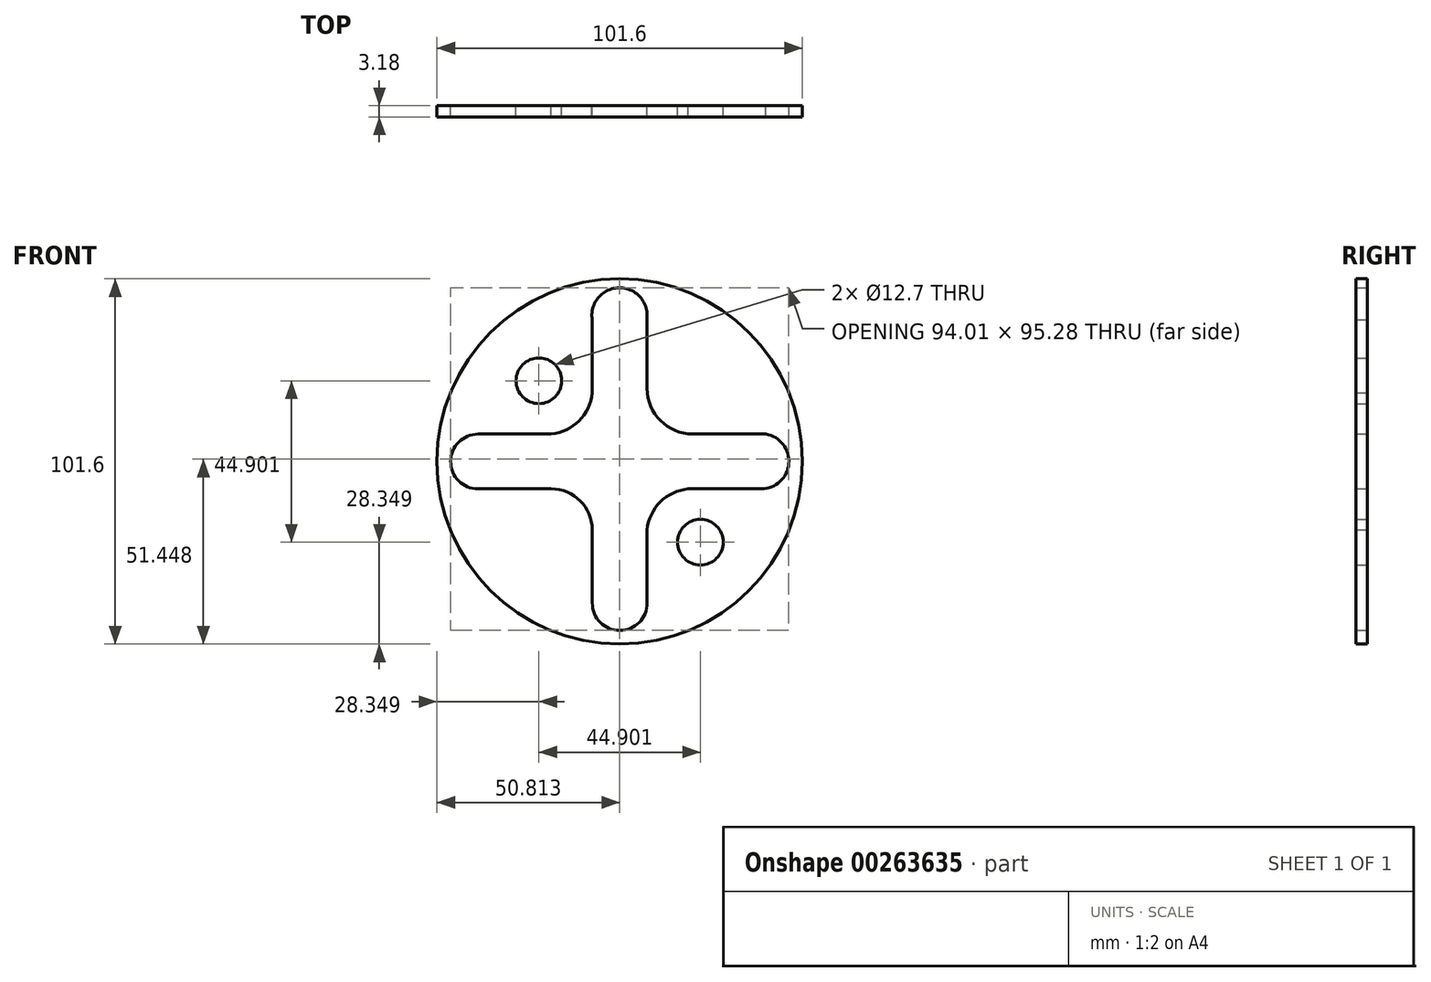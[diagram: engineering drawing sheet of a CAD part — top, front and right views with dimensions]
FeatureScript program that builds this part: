
annotation { "Feature Type Name" : "Feature", "Feature Type Description" : "" }
export const myFeature = defineFeature(function(context is Context, id is Id, definition is map)
    precondition{}
    {
        {
            var Q0;
            Q0=qCreatedBy(makeId("Front.planeOp"),FACE);
            var sketch = newSketch(context, id + "F0", { "sketchPlane" : qUnion([Q0])});
            skCircle(sketch, "E0", {"center": v(0, 0) * mm, "radius": 50.8 * mm});
            skPoint(sketch, "E1", {"position": v(19.05, 0) * mm});
            skPoint(sketch, "E2", {"position": v(-19.05, 0) * mm});
            skLineSegment(sketch, "E3", {"start": v(20.32, 7.62) * mm, "end": v(40.64, 7.62) * mm});
            skLineSegment(sketch, "E4", {"start": v(19.05, -7.62) * mm, "end": v(39.37, -7.62) * mm});
            skLineSegment(sketch, "E5", {"start": v(-19.05, 7.62) * mm, "end": v(-39.37, 7.62) * mm});
            skLineSegment(sketch, "E6", {"start": v(-19.05, -7.62) * mm, "end": v(-39.37, -7.62) * mm});
            skPoint(sketch, "E7", {"position": v(0, -19.05) * mm});
            skPoint(sketch, "E8", {"position": v(0, 19.05) * mm});
            skLineSegment(sketch, "E9", {"start": v(7.62, -19.05) * mm, "end": v(7.62, -39.37) * mm});
            skLineSegment(sketch, "E10", {"start": v(-7.62, -19.05) * mm, "end": v(-7.62, -39.37) * mm});
            skLineSegment(sketch, "E11", {"start": v(-7.62, 19.05) * mm, "end": v(-7.62, 39.37) * mm});
            skLineSegment(sketch, "E12", {"start": v(7.62, 20.32) * mm, "end": v(7.62, 40.64) * mm});
            skArc(sketch, "E13", {"start": v(-39.37, 7.62) * mm, "mid": v(-47, 0) * mm, "end": v(-39.37, -7.62) * mm});
            skArc(sketch, "E14", {"start": v(39.37, -7.62) * mm, "mid": v(47.02, -0.58) * mm, "end": v(40.64, 7.62) * mm});
            skArc(sketch, "E15", {"start": v(-7.62, -39.37) * mm, "mid": v(0, -47) * mm, "end": v(7.62, -39.37) * mm});
            skArc(sketch, "E16", {"start": v(7.62, 40.64) * mm, "mid": v(-0.7, 48.29) * mm, "end": v(-7.62, 39.37) * mm});
            skArc(sketch, "E17", {"start": v(7.62, 20.32) * mm, "mid": v(11.34, 11.34) * mm, "end": v(20.32, 7.62) * mm});
            skArc(sketch, "E18", {"start": v(-19.05, 7.62) * mm, "mid": v(-11.28, 11.28) * mm, "end": v(-7.62, 19.05) * mm});
            skArc(sketch, "E19", {"start": v(19.05, -7.62) * mm, "mid": v(11.28, -11.28) * mm, "end": v(7.62, -19.05) * mm});
            skArc(sketch, "E20", {"start": v(-7.62, -19.05) * mm, "mid": v(-10.97, -10.97) * mm, "end": v(-19.05, -7.62) * mm});
            skLineSegment(sketch, "E21", {"start": v(0, 50.8) * mm, "end": v(0, -50.8) * mm});
            skLineSegment(sketch, "E22", {"start": v(0, 0) * mm, "end": v(-35.92, 35.92) * mm});
            skLineSegment(sketch, "E23", {"start": v(-35.92, 35.92) * mm, "end": v(35.92, -35.92) * mm});
            skLineSegment(sketch, "E24", {"start": v(-35.92, 35.92) * mm, "end": v(-22.45, 22.45) * mm});
            skCircle(sketch, "E25", {"center": v(-22.45, 22.45) * mm, "radius": 6.35 * mm});
            skLineSegment(sketch, "E26", {"start": v(35.92, -35.92) * mm, "end": v(22.45, -22.45) * mm});
            skCircle(sketch, "E27", {"center": v(22.45, -22.45) * mm, "radius": 6.35 * mm});
            skSolve(sketch);
        }
        {
            var Q0;
            Q0 = qSketchRegion(id + "F0", true);
            extrude(context, id + "F1", {"entities" : qUnion([Q0]), "depth" : 3.17 * mm});
        }
    });
